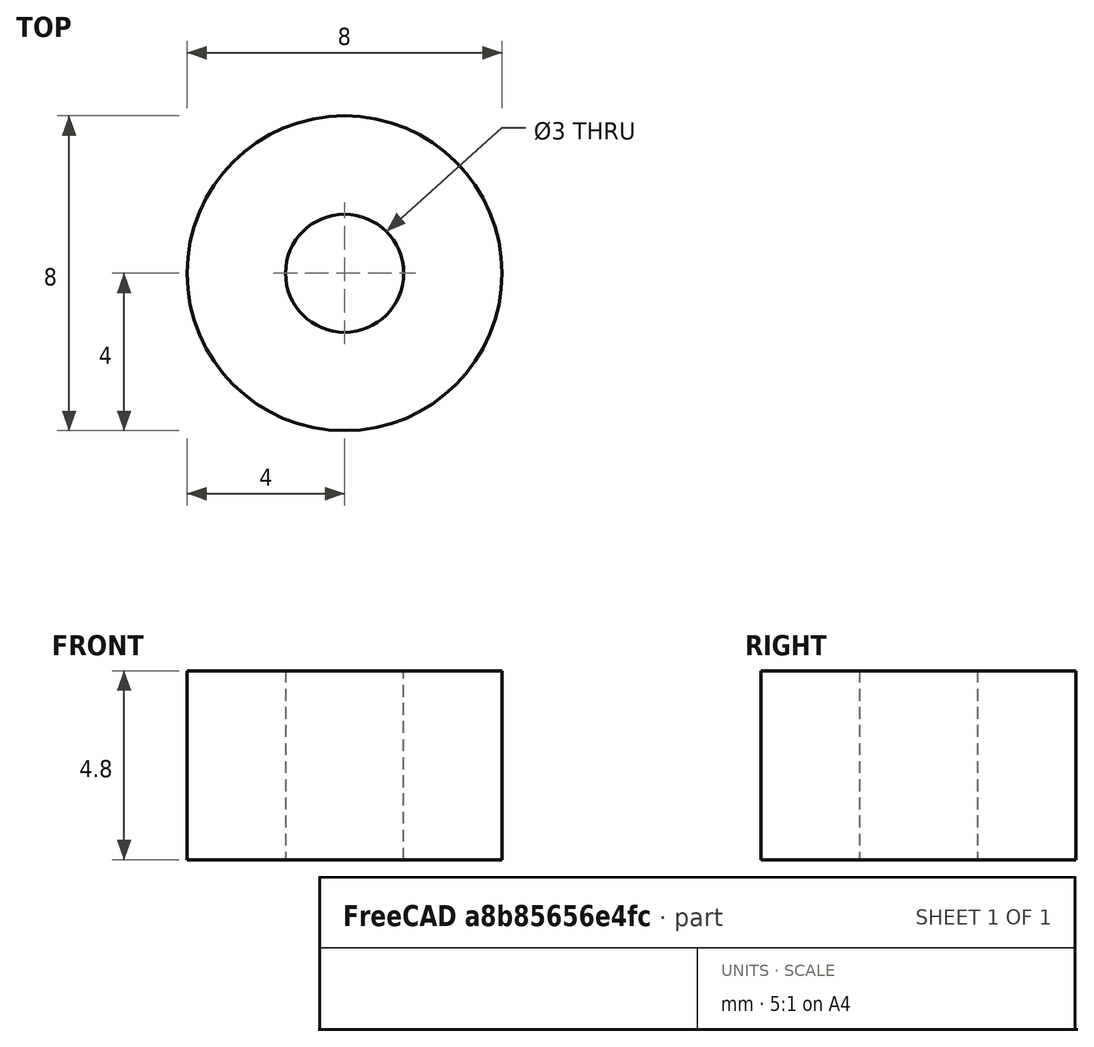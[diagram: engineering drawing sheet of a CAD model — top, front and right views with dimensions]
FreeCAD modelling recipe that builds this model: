
FCSTD DOCUMENT  (FreeCAD 0.20R)
Label: oled_spacers
License: All rights reserved
LicenseURL: http://en.wikipedia.org/wiki/All_rights_reserved
objects: Sketcher::SketchObject×1, PartDesign::Pad×1, PartDesign::Body×1
note: 4 computed .brp shape members not serialized (recipe doc carries the construction recipe); baked Part::Feature solids carry a one-line shape summary decoded from their .brp

FEATURE [Sketcher::SketchObject] Sketch
  FullyConstrained = true
  MapMode = 5
  Support = -> [XY_Plane]
  sketch-geometry (2):
    g0: Circle CenterX=0 CenterY=0 CenterZ=0 NormalX=0 NormalY=0 NormalZ=1 AngleXU=0 Radius=1.5
    g1: Circle CenterX=0 CenterY=0 CenterZ=0 NormalX=0 NormalY=0 NormalZ=1 AngleXU=0 Radius=4
  constraints (4):
    c: Coincident(g0,g-1)
    c: Diameter(g0) = 3
    c: Coincident(g1,g0)
    c: Diameter(g1) = 8
FEATURE [PartDesign::Pad] Pad
  Direction = (0,0,1)
  Length = 4.8
  Length2 = 10
  Profile = -> Sketch
  ReferenceAxis = -> Sketch [N_Axis]
  Type = 0
FEATURE [PartDesign::Body] Body
  Group = -> [Sketch,Pad]
  Origin = -> Origin
  Tip = -> Pad
